# Revit family: Mechanical_Menzies-Metal-Products_SL5000-Bath-Dryer-Vent
name_source: partatom
category: Mechanical Equipment
revit_build: Autodesk Revit 2018 (Build: 20170223_1515(x64)
units: mm (PartAtom-declared; Revit-internal decimal feet)

## family parameters
Cut with Voids When Loaded = No
Host = Face
OmniClass Number = 23.60.30.14
OmniClass Title = Ducting and Wireways for General Use
Part Type = Normal
Room Calculation Point = No
Round Connector Dimension = Use Diameter
Shared = No

## types (1)
- 9" x 20"
    Assembly Code = D2040200
    CW Connection = No
    Custom Size = Standard size shown. Available with up to 12 outlets. Contact manufacturer for more information.
    Default Elevation = 48 "
    Depth = 9 "
    Description = SL5000 Bath-Dryer Vent
    Drain Flow = 0 GPM
    Edition number = 1
    HW Connection = No
    Manufacturer = Menzies Metal Products
    Model = 600-2000
    Product Guid = dd73fe51-8093-4723-9ade-4250b80a0b82
    Product Material = Metal - Menzies Metal Products - Galvanized Steel
    Product data url = https://www.bimobject.com
    URL = https://www.menzies-metal.com
    Vent Connection = No
    Waste Connection = No
    Weight = 17.10 lbf
    Width = 20 "

## geometry (parser evidence)
native form markers: Sweep x7
no freeform markers — native parametric forms only
